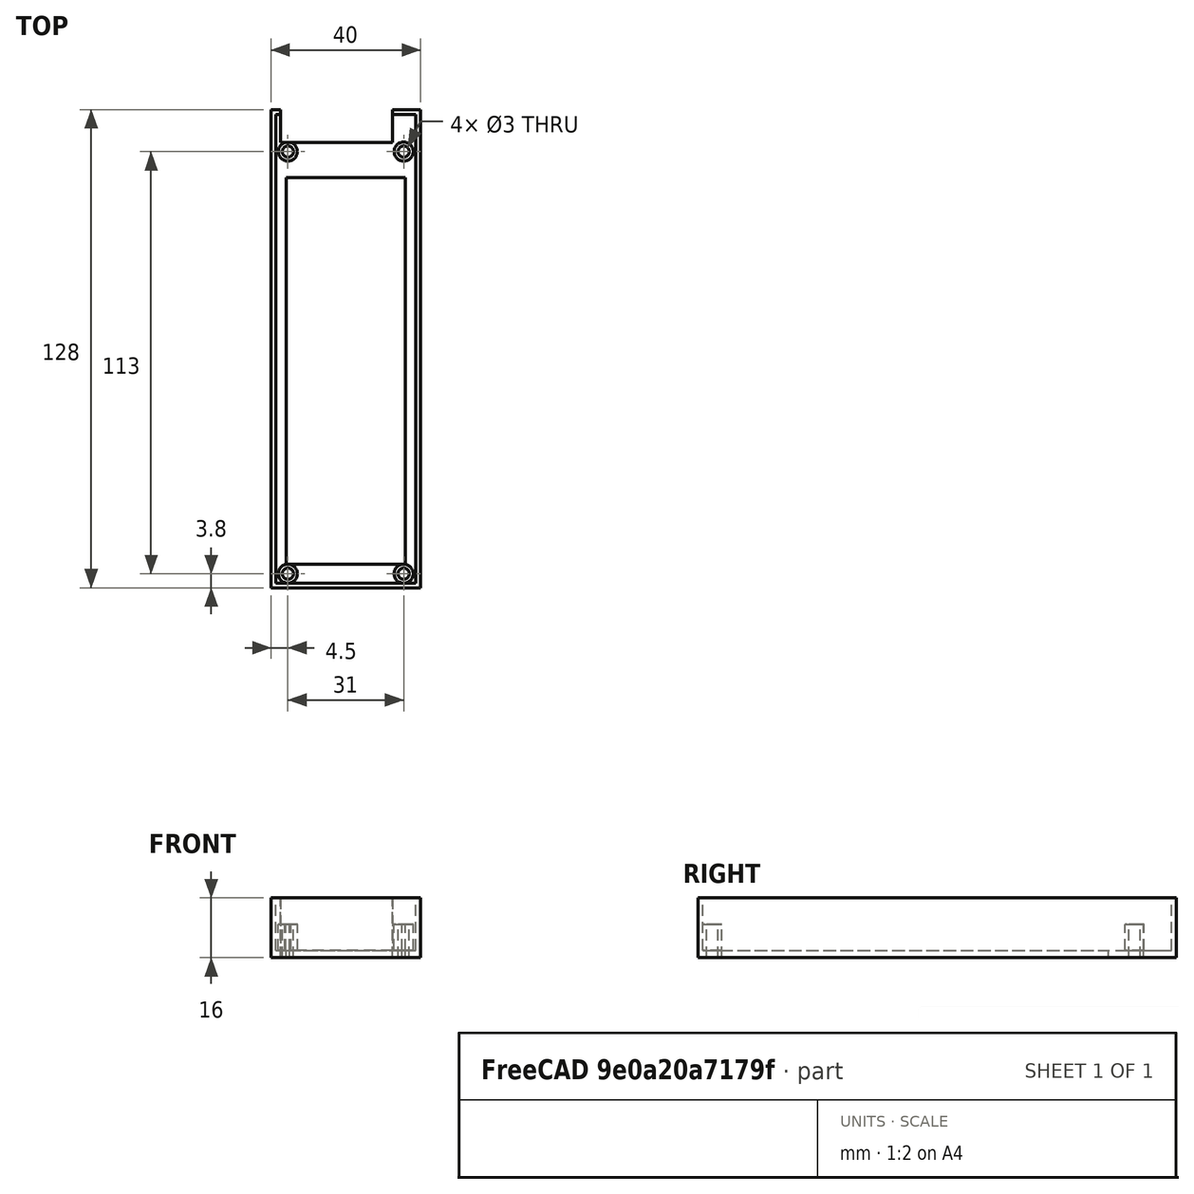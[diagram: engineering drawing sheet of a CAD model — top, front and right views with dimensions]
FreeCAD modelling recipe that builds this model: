
FCSTD DOCUMENT  (FreeCAD 0.18R4 (GitTag))
Label: LCD case-v3
License: All rights reserved
LicenseURL: http://en.wikipedia.org/wiki/All_rights_reserved
objects: Part::FeaturePython×6, Part::Box×4, Part::Cut×4, Part::Cylinder×2, Part::MultiFuse×2
note: 18 computed .brp shape members not serialized (recipe doc carries the construction recipe); baked Part::Feature solids carry a one-line shape summary decoded from their .brp

FEATURE [Part::Box] Box  label="Cube"
  AttacherType = Attacher::AttachEngine3D
  Height = 16
  Length = 40
  Width = 128
FEATURE [Part::Box] Box001  label="Cube001"
  AttacherType = Attacher::AttachEngine3D
  Height = 14
  Length = 37.4
  Placement = pos=(1.3,1.3,2) rot=(0,0,1;0rad)
  Width = 125.4
FEATURE [Part::Box] Box002  label="Screen cutout"
  AttacherType = Attacher::AttachEngine3D
  Height = 2
  Length = 32
  Placement = pos=(4,6.3,0) rot=(0,0,1;0rad)
  Width = 103.5
FEATURE [Part::Cylinder] Cylinder  label="Board post 1"
  Angle = 360
  AttacherType = Attacher::AttachEngine3D
  Height = 9
  Placement = pos=(4.5,3.8,0) rot=(0,0,1;0rad)
  Radius = 2.55
FEATURE [Part::FeaturePython] Clone  label="Board post 2"  # Draft clone (typed FeaturePython)
  AttacherType = Attacher::AttachEngine3D
  Fuse = false
  Objects = -> [Cylinder]
  Placement = pos=(35.5,3.8,0) rot=(0,0,1;0rad)
  Scale = (1,1,1)
FEATURE [Part::FeaturePython] Clone001  label="Board post 3"  # Draft clone (typed FeaturePython)
  AttacherType = Attacher::AttachEngine3D
  Fuse = false
  Objects = -> [Cylinder]
  Placement = pos=(4.5,116.8,0) rot=(0,0,1;0rad)
  Scale = (1,1,1)
FEATURE [Part::FeaturePython] Clone002  label="Board post 4"  # Draft clone (typed FeaturePython)
  AttacherType = Attacher::AttachEngine3D
  Fuse = false
  Objects = -> [Cylinder]
  Placement = pos=(35.5,116.8,0) rot=(0,0,1;0rad)
  Scale = (1,1,1)
FEATURE [Part::Cylinder] Cylinder001  label="Board post drill 1"
  Angle = 360
  AttacherType = Attacher::AttachEngine3D
  Height = 9
  Placement = pos=(4.5,3.8,0) rot=(0,0,1;0rad)
  Radius = 1.5
FEATURE [Part::FeaturePython] Clone003  label="Board post drill 2"  # Draft clone (typed FeaturePython)
  AttacherType = Attacher::AttachEngine3D
  Fuse = false
  Objects = -> [Cylinder001]
  Placement = pos=(35.5,3.8,0) rot=(0,0,1;0rad)
  Scale = (1,1,1)
FEATURE [Part::FeaturePython] Clone004  label="Board post drill 3"  # Draft clone (typed FeaturePython)
  AttacherType = Attacher::AttachEngine3D
  Fuse = false
  Objects = -> [Cylinder001]
  Placement = pos=(4.5,116.8,0) rot=(0,0,1;0rad)
  Scale = (1,1,1)
FEATURE [Part::FeaturePython] Clone005  label="Board post drill 4"  # Draft clone (typed FeaturePython)
  AttacherType = Attacher::AttachEngine3D
  Fuse = false
  Objects = -> [Cylinder001]
  Placement = pos=(35.5,116.8,0) rot=(0,0,1;0rad)
  Scale = (1,1,1)
FEATURE [Part::Box] Box003  label="Connector cutout"
  AttacherType = Attacher::AttachEngine3D
  Height = 16
  Length = 30
  Placement = pos=(2.5,119.2,0) rot=(0,0,1;0rad)
  Width = 8.8
FEATURE [Part::Cut] Cut  label="Main case"
  Base = -> Box
  Tool = -> Box001
FEATURE [Part::Cut] Cut001  label="Main case with screen cutout"
  Base = -> Cut
  Tool = -> Box002
FEATURE [Part::MultiFuse] Fusion001  label="Board drills"
  Shapes = -> [Clone005,Clone003,Clone004,Cylinder001]
FEATURE [Part::MultiFuse] Fusion  label="Case plus board posts"
  Shapes = -> [Cut001,Clone,Clone002,Clone001,Cylinder]
FEATURE [Part::Cut] Cut002  label="Case drilled"
  Base = -> Fusion
  Tool = -> Fusion001
FEATURE [Part::Cut] Cut003  label="Case with connector cutout"
  Base = -> Cut002
  Tool = -> Box003
